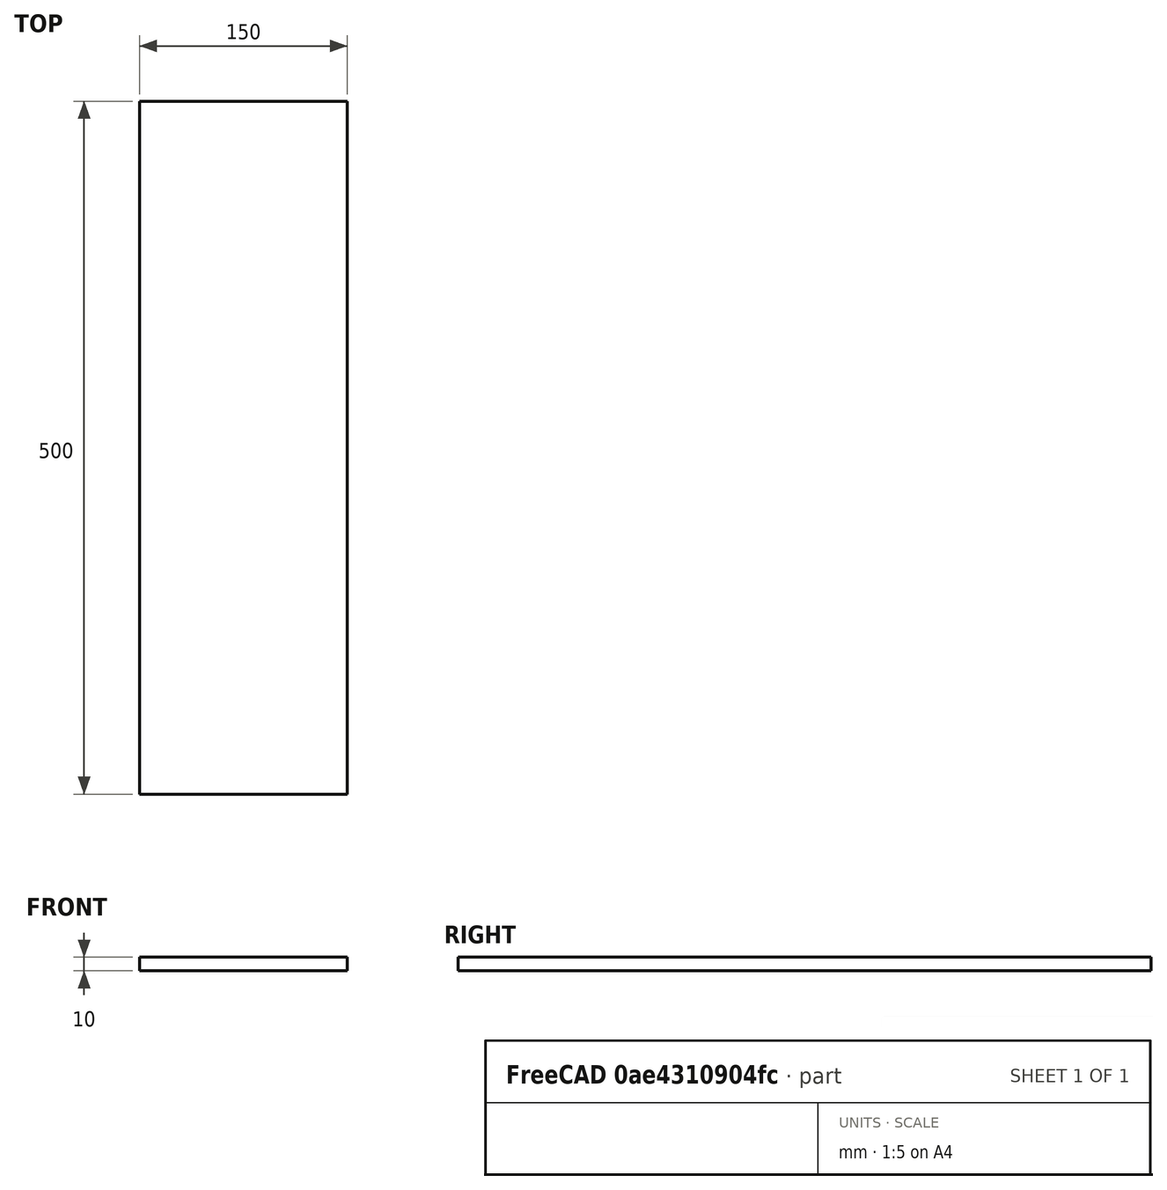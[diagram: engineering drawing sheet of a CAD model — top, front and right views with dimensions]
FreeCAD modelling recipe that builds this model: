
FCSTD DOCUMENT  (FreeCAD 0.18R14555 (Git shallow))
Label: 7002_ASM_Marquee_bottom
License: All rights reserved
LicenseURL: http://en.wikipedia.org/wiki/All_rights_reserved
objects: Sketcher::SketchObject×1, PartDesign::Pad×1, PartDesign::Body×1, Spreadsheet::Sheet×1
note: 4 computed .brp shape members not serialized (recipe doc carries the construction recipe); baked Part::Feature solids carry a one-line shape summary decoded from their .brp

FEATURE [Sketcher::SketchObject] Sketch
  MapMode = 5
  Support = -> [XY_Plane]
  expr: Constraints[6] = xls.k_d
  expr: Constraints[5] = xls.k_w
  sketch-geometry (5):
    g0: LineSegment StartX=0 StartY=500 StartZ=0 EndX=150 EndY=500 EndZ=0
    g1: LineSegment StartX=150 StartY=500 StartZ=0 EndX=150 EndY=0 EndZ=0
    g2: LineSegment StartX=150 StartY=0 StartZ=0 EndX=0 EndY=0 EndZ=0
    g3: LineSegment StartX=0 StartY=0 StartZ=0 EndX=0 EndY=250 EndZ=0
    g4: LineSegment StartX=0 StartY=250 StartZ=0 EndX=0 EndY=500 EndZ=0
  constraints (14):
    c: Coincident(g0,g1)
    c: Coincident(g1,g2)
    c: Horizontal(g0)
    c: Horizontal(g2)
    c: Vertical(g1)
    c: DistanceY(g1,g1) = 500
    c: DistanceX(g0,g0) = 150
    c: Coincident(g3,g2)
    c: Coincident(g4,g0)
    c: Equal(g3,g4)
    c: Vertical(g4)
    c: Vertical(g3)
    c: Coincident(g3,g4)
    c: Coincident(g2,g-1)
FEATURE [PartDesign::Pad] Pad
  Length = 10
  Length2 = 100
  Profile = -> Sketch
  Type = 0
  expr: Length = xls.k_t_0
FEATURE [PartDesign::Body] Body
  Group = -> [Sketch,Pad]
  Origin = -> Origin
  Tip = -> Pad
FEATURE [Spreadsheet::Sheet] Spreadsheet  label="xls"
  cells = B3=KEABOPARD; B4=Thickness; C4=k_t_0; D4(k_t_0)=10; E4=mm; F4=Note:; G4=Plexi is 3mm; B5=Width; C5=k_w; D5(k_w)=500; E5=mm; B6=Deapth; C6=k_d; D6(k_d)=150; E6=mm
